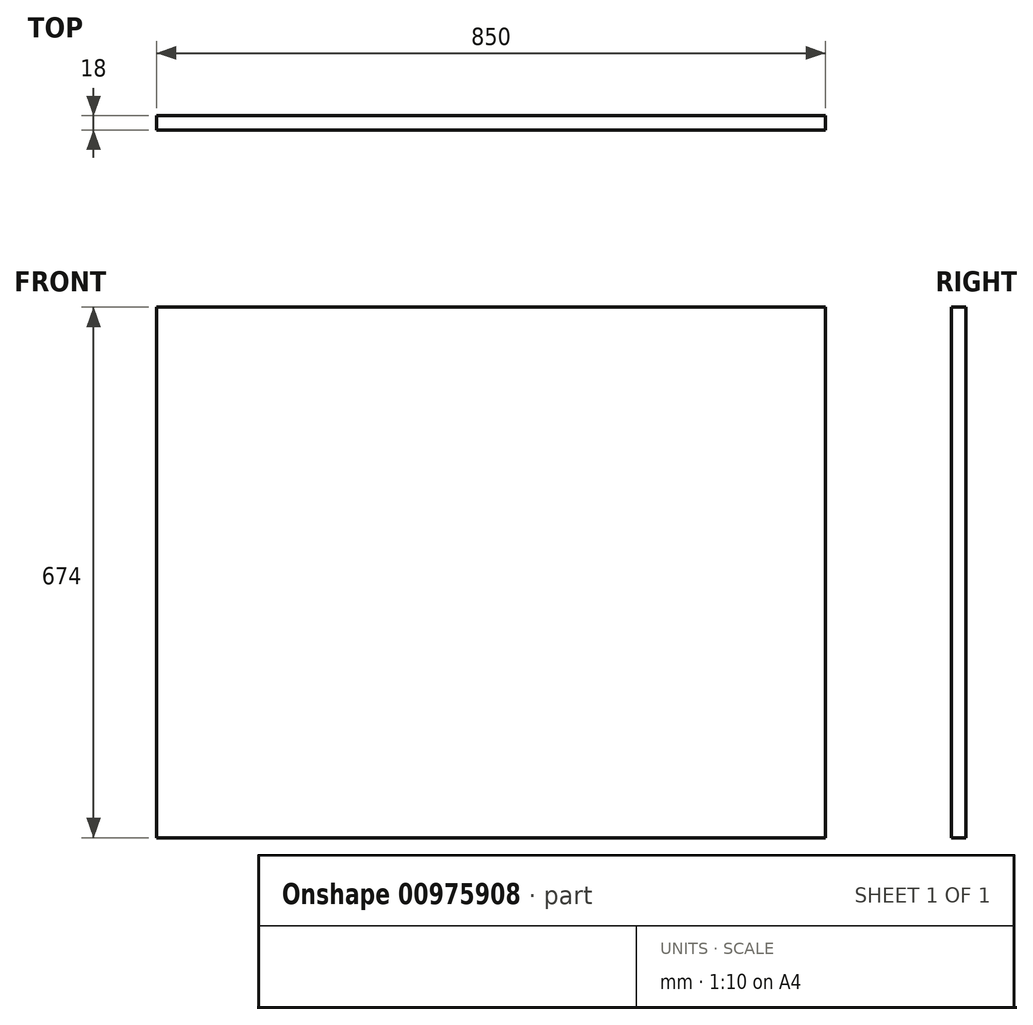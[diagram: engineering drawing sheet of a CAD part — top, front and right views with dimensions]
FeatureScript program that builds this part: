
annotation { "Feature Type Name" : "Feature", "Feature Type Description" : "" }
export const myFeature = defineFeature(function(context is Context, id is Id, definition is map)
    precondition{}
    {
        {
            var Q0;
            Q0=qCreatedBy(makeId("Front.planeOp"),FACE);
            var sketch = newSketch(context, id + "F0", { "sketchPlane" : qUnion([Q0])});
            skLineSegment(sketch, "E0.bottom", {"start": v(-555.5, 635.84) * mm, "end": v(294.5, 635.84) * mm});
            skLineSegment(sketch, "E0.top", {"start": v(-555.5, -38.16) * mm, "end": v(294.5, -38.16) * mm});
            skLineSegment(sketch, "E0.left", {"start": v(-555.5, 635.84) * mm, "end": v(-555.5, -38.16) * mm});
            skLineSegment(sketch, "E0.right", {"start": v(294.5, 635.84) * mm, "end": v(294.5, -38.16) * mm});
            skSolve(sketch);
        }
        {
            var Q0;
            Q0=makeQuery(id+"F0.imprint","IMPRINT",FACE,{"disambiguationData":[TD([[makeQuery(id+"F0.imprint","IMPRINT",EDGE,{"derivedFrom":sQuery(id+"F0.wireOp",EDGE,"E0.bottom")}),-1.0]])]});
            extrude(context, id + "F1", {"entities" : qUnion([Q0]), "depth" : 18 * mm, "offsetDistance" : 25 * mm});
        }
    });
